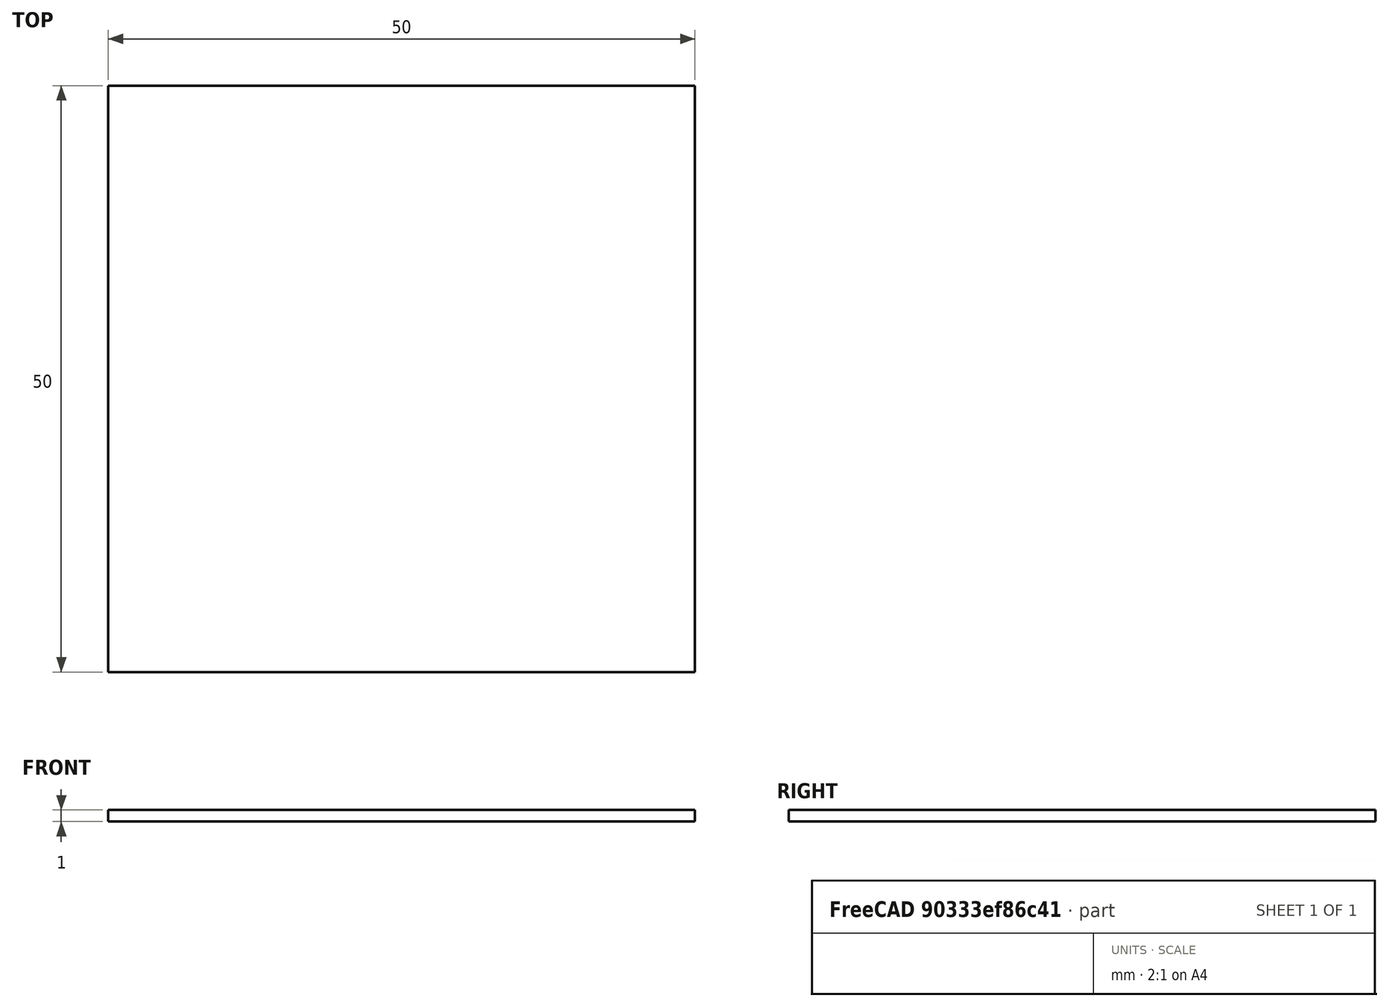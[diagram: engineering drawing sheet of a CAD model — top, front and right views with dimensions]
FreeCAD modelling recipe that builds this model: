
FCSTD DOCUMENT  (FreeCAD 0.20R29177 +233 (Git))
Label: sketch_cuadrado_restricciones
License: Creative Commons Attribution-ShareAlike
LicenseURL: http://creativecommons.org/licenses/by-sa/4.0/
objects: Sketcher::SketchObject×1, Part::Extrusion×1
note: 2 computed .brp shape members not serialized (recipe doc carries the construction recipe); baked Part::Feature solids carry a one-line shape summary decoded from their .brp

FEATURE [Sketcher::SketchObject] Sketch001
  FullyConstrained = true
  sketch-geometry (4):
    g0: LineSegment StartX=50 StartY=0 StartZ=0 EndX=50 EndY=50 EndZ=0
    g1: LineSegment StartX=50 StartY=50 StartZ=0 EndX=0 EndY=50 EndZ=0
    g2: LineSegment StartX=0 StartY=50 StartZ=0 EndX=0 EndY=0 EndZ=0
    g3: LineSegment StartX=0 StartY=0 StartZ=0 EndX=50 EndY=0 EndZ=0
  constraints (11):
    c: Coincident(g0,g1)
    c: Coincident(g1,g2)
    c: Coincident(g3,g2)
    c: Coincident(g0,g3)
    c: Horizontal(g3)
    c: Horizontal(g1)
    c: Vertical(g0)
    c: Vertical(g2)
    c: DistanceX(g1,g1) = 50
    c: DistanceY(g0,g0) = 50
    c: Coincident(g2,g-1)
FEATURE [Part::Extrusion] Extrude
  Base = -> Sketch001
  Dir = (0,0,1)
  DirMode = 0
  FaceMakerClass = Part::FaceMakerBullseye
  LengthFwd = 5
  LengthRev = -4
  Placement = pos=(0,0,-4) rot=(0,0,1;0rad)
  Solid = false
  Symmetric = false
